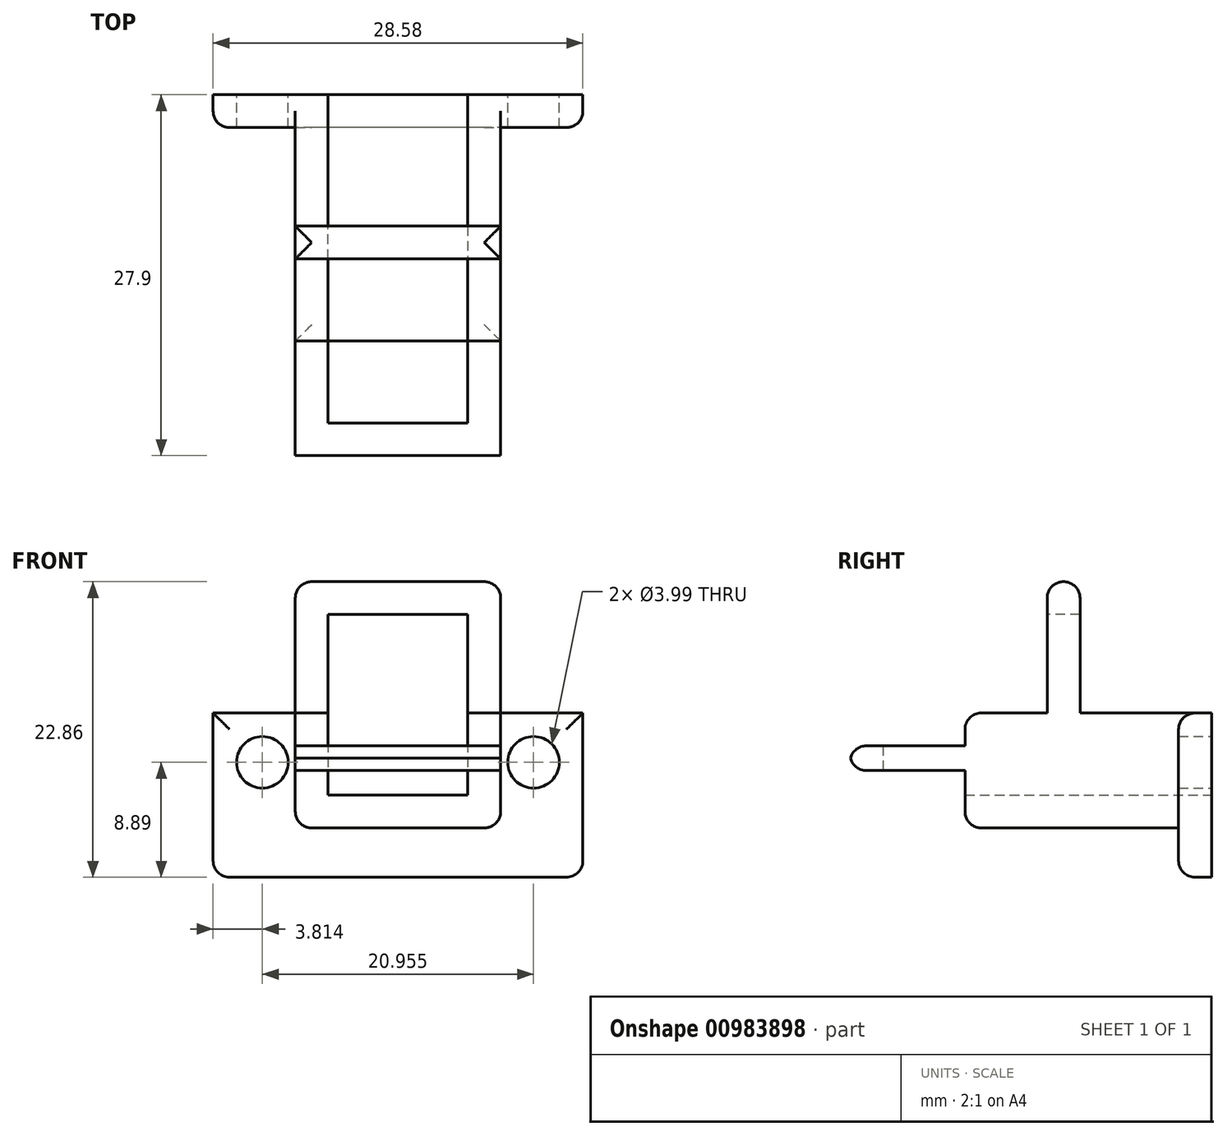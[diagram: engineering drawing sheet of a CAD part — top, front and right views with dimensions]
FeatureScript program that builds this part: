
annotation { "Feature Type Name" : "Feature", "Feature Type Description" : "" }
export const myFeature = defineFeature(function(context is Context, id is Id, definition is map)
    precondition{}
    {
        {
            var Q0;
            Q0=qCreatedBy(makeId("Front.planeOp"),FACE);
            var sketch = newSketch(context, id + "F0", { "sketchPlane" : qUnion([Q0])});
            skLineSegment(sketch, "E0", {"start": v(-23.2, 0) * mm, "end": v(-23.2, -6.35) * mm});
            skLineSegment(sketch, "E1", {"start": v(-12.41, 0) * mm, "end": v(-12.41, -6.35) * mm});
            skLineSegment(sketch, "E2", {"start": v(-23.2, -6.35) * mm, "end": v(-12.41, -6.35) * mm});
            skLineSegment(sketch, "E3", {"start": v(-12.41, 0) * mm, "end": v(-9.87, 0) * mm});
            skLineSegment(sketch, "E4", {"start": v(-9.87, 0) * mm, "end": v(-9.87, -8.89) * mm});
            skLineSegment(sketch, "E5", {"start": v(-9.87, -8.89) * mm, "end": v(-25.75, -8.89) * mm});
            skLineSegment(sketch, "E6", {"start": v(-25.75, -8.89) * mm, "end": v(-25.75, 0) * mm});
            skLineSegment(sketch, "E7", {"start": v(-25.75, 0) * mm, "end": v(-23.2, 0) * mm});
            skLineSegment(sketch, "E8", {"start": v(-9.87, 0) * mm, "end": v(-3.52, 0) * mm});
            skLineSegment(sketch, "E9", {"start": v(-3.52, 0) * mm, "end": v(-3.52, -12.7) * mm});
            skLineSegment(sketch, "E10", {"start": v(-3.52, -12.7) * mm, "end": v(-32.1, -12.7) * mm});
            skLineSegment(sketch, "E11", {"start": v(-32.1, -12.7) * mm, "end": v(-32.1, 0) * mm});
            skLineSegment(sketch, "E12", {"start": v(-32.1, 0) * mm, "end": v(-25.75, 0) * mm});
            skCircle(sketch, "E13", {"center": v(-28.29, -3.81) * mm, "radius": 2 * mm});
            skCircle(sketch, "E14", {"center": v(-7.33, -3.81) * mm, "radius": 2 * mm});
            skSolve(sketch);
        }
        {
            var Q0;
            Q0=makeQuery(id+"F0.imprint","IMPRINT",FACE,{"disambiguationData":[TD([[makeQuery(id+"F0.imprint","IMPRINT",EDGE,{"derivedFrom":sQuery(id+"F0.wireOp",EDGE,"E0")}),-1.0]])]});
            extrude(context, id + "F1", {"entities" : qUnion([Q0]), "depth" : 19.05 * mm, "offsetDistance" : 25.4 * mm});
        }
        {
            var Q0;
            Q0=makeQuery(id+"F0.imprint","IMPRINT",FACE,{"disambiguationData":[TD([[makeQuery(id+"F0.imprint","IMPRINT",EDGE,{"derivedFrom":sQuery(id+"F0.wireOp",EDGE,"E4")}),1.0]])]});
            extrude(context, id + "F2", {"entities" : qUnion([Q0]), "operationType" : NewBodyOperationType.ADD, "depth" : 2.54 * mm, "offsetDistance" : 25.4 * mm});
        }
        {
            var Q0;
            Q0=makeQuery(id+"F1.opExtrude","CAP_FACE",FACE,{"disambiguationData":[OSD([sQuery(id+"F0.wireOp",EDGE,"E0"),sQuery(id+"F0.wireOp",EDGE,"E1"),sQuery(id+"F0.wireOp",EDGE,"E2"),sQuery(id+"F0.wireOp",EDGE,"E3"),sQuery(id+"F0.wireOp",EDGE,"E4"),sQuery(id+"F0.wireOp",EDGE,"E5"),sQuery(id+"F0.wireOp",EDGE,"E6"),sQuery(id+"F0.wireOp",EDGE,"E7")])],"isStart":false});
            var sketch = newSketch(context, id + "F3", { "sketchPlane" : qUnion([Q0])});
            skLineSegment(sketch, "E15", {"start": v(-25.75, -2.54) * mm, "end": v(-9.87, -2.54) * mm});
            skLineSegment(sketch, "E16", {"start": v(-9.87, -2.54) * mm, "end": v(-9.87, -4.45) * mm});
            skLineSegment(sketch, "E17", {"start": v(-9.87, -4.45) * mm, "end": v(-25.75, -4.45) * mm});
            skSolve(sketch);
        }
        {
            var Q0;
            {var subQ0=sQuery(id+"F3.wireOp",EDGE,"E16");Q0=makeQuery(id+"F3.imprint","IMPRINT",FACE,{"disambiguationData":[TD([[makeQuery(id+"F3.imprint","IMPRINT",EDGE,{"derivedFrom":subQ0}),-1.0]])]});}
            var Q1;
            {var subQ0=sQuery(id+"F3.wireOp",EDGE,"E15");var subQ1=makeQuery(id+"F1.opExtrude","CAP_EDGE",EDGE,{"disambiguationData":[OSD([sQuery(id+"F0.wireOp",EDGE,"E6")])],"isStart":false});var subQ2=makeQuery(id+"F3.imprint","INTERSECT",VERTEX,{"derivedFrom":[subQ1,subQ0]});Q1=makeQuery(id+"F3.imprint","IMPRINT",FACE,{"disambiguationData":[TD([[makeQuery(id+"F3.imprint","IMPRINT",EDGE,{"disambiguationData":[TD([[subQ2,-1.0]])],"derivedFrom":subQ0}),-1.0]])]});}
            extrude(context, id + "F4", {"entities" : qUnion([Q0, Q1]), "operationType" : NewBodyOperationType.ADD, "depth" : 8.9 * mm, "offsetDistance" : 25.4 * mm});
        }
        {
            var Q0;
            {var subQ0=sQuery(id+"F0.wireOp",EDGE,"E1");Q0=makeQuery(id+"F4.boolean.opBoolean","MERGE",FACE,{"derivedFrom":[makeQuery(id+"F1.opExtrude","SWEPT_FACE",FACE,{"disambiguationData":[OSD([subQ0])]}),makeQuery(id+"F4.opExtrude","SWEPT_FACE",FACE,{"disambiguationData":[OSD([subQ0])]})]});}
            var sketch = newSketch(context, id + "F5", { "sketchPlane" : qUnion([Q0])});
            skLineSegment(sketch, "E18", {"start": v(25.4, -2.54) * mm, "end": v(25.4, -4.44) * mm});
            skSolve(sketch);
        }
        {
            var Q0;
            {var subQ0=sQuery(id+"F5.wireOp",EDGE,"E18");Q0=makeQuery(id+"F5.imprint","IMPRINT",FACE,{"disambiguationData":[TD([[makeQuery(id+"F5.imprint","IMPRINT",EDGE,{"derivedFrom":subQ0}),1.0]])]});}
            extrude(context, id + "F6", {"entities" : qUnion([Q0]), "operationType" : NewBodyOperationType.ADD, "depth" : 11.43 * mm, "offsetDistance" : 25.4 * mm});
        }
        {
            var Q0;
            Q0=makeQuery(id+"F2.boolean.opBoolean","MERGE",FACE,{"derivedFrom":[makeQuery(id+"F1.opExtrude","SWEPT_FACE",FACE,{"disambiguationData":[OSD([sQuery(id+"F0.wireOp",EDGE,"E7")])]}),makeQuery(id+"F2.opExtrude","SWEPT_FACE",FACE,{"disambiguationData":[OSD([sQuery(id+"F0.wireOp",EDGE,"E12")])]})]});
            var sketch = newSketch(context, id + "F7", { "sketchPlane" : qUnion([Q0])});
            skLineSegment(sketch, "E19", {"start": v(-25.75, -10.16) * mm, "end": v(-23.2, -10.16) * mm});
            skLineSegment(sketch, "E20", {"start": v(-25.75, -12.7) * mm, "end": v(-23.2, -12.7) * mm});
            skSolve(sketch);
        }
        {
            var Q0;
            Q0=makeQuery(id+"F2.boolean.opBoolean","MERGE",FACE,{"derivedFrom":[makeQuery(id+"F1.opExtrude","SWEPT_FACE",FACE,{"disambiguationData":[OSD([sQuery(id+"F0.wireOp",EDGE,"E3")])]}),makeQuery(id+"F2.opExtrude","SWEPT_FACE",FACE,{"disambiguationData":[OSD([sQuery(id+"F0.wireOp",EDGE,"E8")])]})]});
            var sketch = newSketch(context, id + "F8", { "sketchPlane" : qUnion([Q0])});
            skLineSegment(sketch, "E21", {"start": v(-12.41, -12.7) * mm, "end": v(-9.87, -12.7) * mm});
            skLineSegment(sketch, "E22", {"start": v(-12.41, -10.16) * mm, "end": v(-9.87, -10.16) * mm});
            skSolve(sketch);
        }
        {
            var Q0;
            {var subQ0=sQuery(id+"F7.wireOp",EDGE,"E19");Q0=makeQuery(id+"F7.imprint","IMPRINT",FACE,{"disambiguationData":[TD([[makeQuery(id+"F7.imprint","IMPRINT",EDGE,{"derivedFrom":subQ0}),-1.0]])]});}
            var Q1;
            {var subQ0=sQuery(id+"F8.wireOp",EDGE,"E21");Q1=makeQuery(id+"F8.imprint","IMPRINT",FACE,{"disambiguationData":[TD([[makeQuery(id+"F8.imprint","IMPRINT",EDGE,{"derivedFrom":subQ0}),1.0]])]});}
            extrude(context, id + "F9", {"entities" : qUnion([Q0, Q1]), "operationType" : NewBodyOperationType.ADD, "depth" : 10.16 * mm, "offsetDistance" : 25.4 * mm});
        }
        {
            var Q0;
            {var subQ0=sQuery(id+"F0.wireOp",EDGE,"E0");Q0=makeQuery(id+"F9.boolean.opBoolean","MERGE",FACE,{"derivedFrom":[makeQuery(id+"F4.boolean.opBoolean","MERGE",FACE,{"derivedFrom":[makeQuery(id+"F1.opExtrude","SWEPT_FACE",FACE,{"disambiguationData":[OSD([subQ0])]}),makeQuery(id+"F4.opExtrude","SWEPT_FACE",FACE,{"disambiguationData":[OSD([subQ0])]})]}),makeQuery(id+"F9.opExtrude","SWEPT_FACE",FACE,{"disambiguationData":[OSD([subQ0,sQuery(id+"F0.wireOp",EDGE,"E7")])]})]});}
            var sketch = newSketch(context, id + "F10", { "sketchPlane" : qUnion([Q0])});
            skLineSegment(sketch, "E23", {"start": v(-12.7, 7.62) * mm, "end": v(-10.16, 7.62) * mm});
            skSolve(sketch);
        }
        {
            var Q0;
            {var subQ0=sQuery(id+"F10.wireOp",EDGE,"E23");Q0=makeQuery(id+"F10.imprint","IMPRINT",FACE,{"disambiguationData":[TD([[makeQuery(id+"F10.imprint","IMPRINT",EDGE,{"derivedFrom":subQ0}),1.0]])]});}
            extrude(context, id + "F11", {"entities" : qUnion([Q0]), "operationType" : NewBodyOperationType.ADD, "depth" : 11.43 * mm, "offsetDistance" : 25.4 * mm});
        }
        {
            var Q0;
            Q0=makeQuery(id+"F2.opExtrude","CAP_EDGE",EDGE,{"disambiguationData":[OSD([sQuery(id+"F0.wireOp",EDGE,"E12")])],"isStart":false});
            var Q1;
            Q1=makeQuery(id+"F2.opExtrude","CAP_EDGE",EDGE,{"disambiguationData":[OSD([sQuery(id+"F0.wireOp",EDGE,"E11")])],"isStart":false});
            var Q2;
            Q2=makeQuery(id+"F2.opExtrude","CAP_EDGE",EDGE,{"disambiguationData":[OSD([sQuery(id+"F0.wireOp",EDGE,"E10")])],"isStart":false});
            var Q3;
            Q3=makeQuery(id+"F2.opExtrude","CAP_EDGE",EDGE,{"disambiguationData":[OSD([sQuery(id+"F0.wireOp",EDGE,"E8")])],"isStart":false});
            var Q4;
            Q4=makeQuery(id+"F2.opExtrude","SWEPT_EDGE",EDGE,{"disambiguationData":[OSD([sQuery(id+"F0.wireOp",EDGE,"E9"),sQuery(id+"F0.wireOp",EDGE,"E10")])]});
            var Q5;
            Q5=makeQuery(id+"F2.opExtrude","SWEPT_EDGE",EDGE,{"disambiguationData":[OSD([sQuery(id+"F0.wireOp",EDGE,"E10"),sQuery(id+"F0.wireOp",EDGE,"E11")])]});
            var Q6;
            Q6=makeQuery(id+"F2.opExtrude","CAP_EDGE",EDGE,{"disambiguationData":[OSD([sQuery(id+"F0.wireOp",EDGE,"E9")])],"isStart":false});
            var Q7;
            Q7=makeQuery(id+"F1.opExtrude","SWEPT_EDGE",EDGE,{"disambiguationData":[OSD([sQuery(id+"F0.wireOp",EDGE,"E4"),sQuery(id+"F0.wireOp",EDGE,"E5")])]});
            var Q8;
            Q8=makeQuery(id+"F1.opExtrude","SWEPT_EDGE",EDGE,{"disambiguationData":[OSD([sQuery(id+"F0.wireOp",EDGE,"E5"),sQuery(id+"F0.wireOp",EDGE,"E6")])]});
            var Q9;
            {var subQ0=sQuery(id+"F3.wireOp",EDGE,"E15");var subQ1=sQuery(id+"F0.wireOp",EDGE,"E1");Q9=makeQuery(id+"F6.boolean.opBoolean","MERGE",EDGE,{"derivedFrom":[makeQuery(id+"F4.opExtrude","CAP_EDGE",EDGE,{"disambiguationData":[OSD([subQ0]),TDD([makeQuery(id+"F3.imprint","IMPRINT",EDGE,{"disambiguationData":[TD([[makeQuery(id+"F3.imprint","INTERSECT",VERTEX,{"derivedFrom":[makeQuery(id+"F1.opExtrude","CAP_EDGE",EDGE,{"disambiguationData":[OSD([sQuery(id+"F0.wireOp",EDGE,"E6")])],"isStart":false}),subQ0]}),-1.0]])],"derivedFrom":subQ0})])],"isStart":false}),makeQuery(id+"F4.opExtrude","CAP_EDGE",EDGE,{"disambiguationData":[OSD([subQ0]),TDD([makeQuery(id+"F3.imprint","IMPRINT",EDGE,{"disambiguationData":[TD([[makeQuery(id+"F3.imprint","INTERSECT",VERTEX,{"derivedFrom":[makeQuery(id+"F1.opExtrude","CAP_EDGE",EDGE,{"disambiguationData":[OSD([subQ1])],"isStart":false}),subQ0]}),-1.0]])],"derivedFrom":subQ0})])],"isStart":false}),makeQuery(id+"F6.opExtrude","SWEPT_EDGE",EDGE,{"disambiguationData":[OSD([subQ1,subQ0])]})]});}
            var Q10;
            Q10=makeQuery(id+"F1.opExtrude","CAP_EDGE",EDGE,{"disambiguationData":[OSD([sQuery(id+"F0.wireOp",EDGE,"E5")])],"isStart":false});
            var Q11;
            {var subQ0=sQuery(id+"F3.wireOp",EDGE,"E17");var subQ1=sQuery(id+"F0.wireOp",EDGE,"E1");Q11=makeQuery(id+"F6.boolean.opBoolean","MERGE",EDGE,{"derivedFrom":[makeQuery(id+"F4.opExtrude","CAP_EDGE",EDGE,{"disambiguationData":[OSD([subQ0]),TDD([makeQuery(id+"F3.imprint","IMPRINT",EDGE,{"disambiguationData":[TD([[makeQuery(id+"F3.imprint","INTERSECT",VERTEX,{"derivedFrom":[makeQuery(id+"F1.opExtrude","CAP_EDGE",EDGE,{"disambiguationData":[OSD([subQ1])],"isStart":false}),subQ0]}),1.0]])],"derivedFrom":subQ0})])],"isStart":false}),makeQuery(id+"F4.opExtrude","CAP_EDGE",EDGE,{"disambiguationData":[OSD([subQ0]),TDD([makeQuery(id+"F3.imprint","IMPRINT",EDGE,{"disambiguationData":[TD([[makeQuery(id+"F3.imprint","INTERSECT",VERTEX,{"derivedFrom":[makeQuery(id+"F1.opExtrude","CAP_EDGE",EDGE,{"disambiguationData":[OSD([sQuery(id+"F0.wireOp",EDGE,"E6")])],"isStart":false}),subQ0]}),1.0]])],"derivedFrom":subQ0})])],"isStart":false}),makeQuery(id+"F6.opExtrude","SWEPT_EDGE",EDGE,{"disambiguationData":[OSD([subQ1,subQ0])]})]});}
            var Q12;
            {var subQ0=sQuery(id+"F7.wireOp",EDGE,"E20");Q12=makeQuery(id+"F11.boolean.opBoolean","MERGE",EDGE,{"derivedFrom":[makeQuery(id+"F9.opExtrude","CAP_EDGE",EDGE,{"disambiguationData":[OSD([subQ0])],"isStart":false}),makeQuery(id+"F9.opExtrude","CAP_EDGE",EDGE,{"disambiguationData":[OSD([sQuery(id+"F8.wireOp",EDGE,"E21")])],"isStart":false}),makeQuery(id+"F11.opExtrude","SWEPT_EDGE",EDGE,{"disambiguationData":[OSD([sQuery(id+"F0.wireOp",EDGE,"E0"),sQuery(id+"F0.wireOp",EDGE,"E7"),subQ0])]})]});}
            var Q13;
            {var subQ0=sQuery(id+"F7.wireOp",EDGE,"E19");Q13=makeQuery(id+"F11.boolean.opBoolean","MERGE",EDGE,{"derivedFrom":[makeQuery(id+"F9.opExtrude","CAP_EDGE",EDGE,{"disambiguationData":[OSD([subQ0])],"isStart":false}),makeQuery(id+"F9.opExtrude","CAP_EDGE",EDGE,{"disambiguationData":[OSD([sQuery(id+"F8.wireOp",EDGE,"E22")])],"isStart":false}),makeQuery(id+"F11.opExtrude","SWEPT_EDGE",EDGE,{"disambiguationData":[OSD([sQuery(id+"F0.wireOp",EDGE,"E0"),sQuery(id+"F0.wireOp",EDGE,"E7"),subQ0])]})]});}
            var Q14;
            Q14=makeQuery(id+"F1.opExtrude","CAP_EDGE",EDGE,{"disambiguationData":[OSD([sQuery(id+"F0.wireOp",EDGE,"E7")])],"isStart":false});
            var Q15;
            Q15=makeQuery(id+"F1.opExtrude","CAP_EDGE",EDGE,{"disambiguationData":[OSD([sQuery(id+"F0.wireOp",EDGE,"E3")])],"isStart":false});
            var Q16;
            Q16=makeQuery(id+"F9.opExtrude","CAP_EDGE",EDGE,{"disambiguationData":[OSD([sQuery(id+"F0.wireOp",EDGE,"E6"),sQuery(id+"F0.wireOp",EDGE,"E7"),sQuery(id+"F0.wireOp",EDGE,"E12")])],"isStart":false});
            var Q17;
            Q17=makeQuery(id+"F9.opExtrude","CAP_EDGE",EDGE,{"disambiguationData":[OSD([sQuery(id+"F0.wireOp",EDGE,"E3"),sQuery(id+"F0.wireOp",EDGE,"E4"),sQuery(id+"F0.wireOp",EDGE,"E8")])],"isStart":false});
            fillet(context, id + "F12", {"entities" : qUnion([Q0, Q1, Q2, Q3, Q4, Q5, Q6, Q7, Q8, Q9, Q10, Q11, Q12, Q13, Q14, Q15, Q16, Q17]), "radius" : 1.27 * mm, "tangentPropagation" : true, "allowEdgeOverflow" : false});
        }
    });
